# Revit family: console with cutout for bowl without tap hole
name_source: partatom
category: Furniture
units: mm (PartAtom-declared; Revit-internal decimal feet)

## family parameters
Always vertical = No
Cut with Voids When Loaded = No
OmniClass Number = 23.21.19.15.33.13
Room Calculation Point = No
Shared = Yes
Work Plane-Based = No

## types (40) — shared parameters
BIMOBJECT = Sanitary: Compound units
CATALOG = Hansgrohe
DESIGN = Germany
ETIM = EC011381 | Bathroom furniture set
IFC = Furnishing element
MASTERFORMAT = 12 35 30.23 | Bathroom Casework
Manufacturer = Hansgrohe
NBSYN = $BASENUMBER.-$ARTNR.-$SURFACE.-$LODLEVEL.
NN = Console with cutout for bowl without tap hole
OBJECTTYPE = Object (single object)
OMNICLASS = 23-19 31 17 11 | Bathroom Units
PRODUCTFAMILY = Xelu Q
PRODUCTGROUP = console
PRODUCTURL = https://pro.hansgrohe.com
R = 75
REGIONSET = Worldwide
UNICLASS2015 = Pr_40_20_76_94 | Vanity units
UNIFORMATII = E2010 | Fixed Furnishings
UNSPSC = 56 | Furniture and Furnishings

## per-type parameters (varying)
| type | ARTNR | BASENUMBER | GTINCODE | L | LINA | LL | LODLEVEL | Model | NAME | NB | PERMALINK | SPECIFICATION | SURFACE | WEIGHT |
| Console 1180_550 with cutout in the middle for bowl without tap hole-54115050-GLOSSY_WHITE-200 | 54115050 | Console 1180/550 with cutout in the middle for bowl without tap hole | 4059625457450 | 1180 | Console 1180/550 with cutout in the middle for bowl without tap hole-54115050-GLOSSY_WHITE-200 | 590 | 200 | Console 1180/550 with cutout in the middle for bowl without tap hole-54115050-GLOSSY_WHITE-200 | Xelu Q Console 1180/550 with cutout in the middle for bowl without tap hole | Console 1180/550 with cutout in the middle for bowl without tap hole-54115050-GLOSSY_WHITE-200 | 54115XXX | Surfaces:    - 54115050 High Gloss White  - 54115910 Diamond Matt Grey  - 54115230 Natural Oak  - 54115630 Dark Walnut      Specification: | GLOSSY_WHITE | 14.5 |
| Console 1180_550 with cutout in the middle for bowl without tap hole-54115050-GLOSSY_WHITE-400 | 54115050 | Console 1180/550 with cutout in the middle for bowl without tap hole | 4059625457450 | 1180 | Console 1180/550 with cutout in the middle for bowl without tap hole-54115050-GLOSSY_WHITE-400 | 590 | 400 | Console 1180/550 with cutout in the middle for bowl without tap hole-54115050-GLOSSY_WHITE-400 | Xelu Q Console 1180/550 with cutout in the middle for bowl without tap hole | Console 1180/550 with cutout in the middle for bowl without tap hole-54115050-GLOSSY_WHITE-400 | 54115XXX | Surfaces:    - 54115050 High Gloss White  - 54115910 Diamond Matt Grey  - 54115230 Natural Oak  - 54115630 Dark Walnut      Specification: | GLOSSY_WHITE | 14.5 |
| Console 1180_550 with cutout in the middle for bowl without tap hole-54115230-NATURAL_OAK-200 | 54115230 | Console 1180/550 with cutout in the middle for bowl without tap hole | 4059625457450 | 1180 | Console 1180/550 with cutout in the middle for bowl without tap hole-54115230-NATURAL_OAK-200 | 590 | 200 | Console 1180/550 with cutout in the middle for bowl without tap hole-54115230-NATURAL_OAK-200 | Xelu Q Console 1180/550 with cutout in the middle for bowl without tap hole | Console 1180/550 with cutout in the middle for bowl without tap hole-54115230-NATURAL_OAK-200 | 54115XXX | Surfaces:    - 54115050 High Gloss White  - 54115910 Diamond Matt Grey  - 54115230 Natural Oak  - 54115630 Dark Walnut      Specification: | NATURAL_OAK | 14.5 |
| Console 1180_550 with cutout in the middle for bowl without tap hole-54115230-NATURAL_OAK-400 | 54115230 | Console 1180/550 with cutout in the middle for bowl without tap hole | 4059625457450 | 1180 | Console 1180/550 with cutout in the middle for bowl without tap hole-54115230-NATURAL_OAK-400 | 590 | 400 | Console 1180/550 with cutout in the middle for bowl without tap hole-54115230-NATURAL_OAK-400 | Xelu Q Console 1180/550 with cutout in the middle for bowl without tap hole | Console 1180/550 with cutout in the middle for bowl without tap hole-54115230-NATURAL_OAK-400 | 54115XXX | Surfaces:    - 54115050 High Gloss White  - 54115910 Diamond Matt Grey  - 54115230 Natural Oak  - 54115630 Dark Walnut      Specification: | NATURAL_OAK | 14.5 |
| Console 1180_550 with cutout in the middle for bowl without tap hole-54115630-DARK_WALNUT-200 | 54115630 | Console 1180/550 with cutout in the middle for bowl without tap hole | 4059625457450 | 1180 | Console 1180/550 with cutout in the middle for bowl without tap hole-54115630-DARK_WALNUT-200 | 590 | 200 | Console 1180/550 with cutout in the middle for bowl without tap hole-54115630-DARK_WALNUT-200 | Xelu Q Console 1180/550 with cutout in the middle for bowl without tap hole | Console 1180/550 with cutout in the middle for bowl without tap hole-54115630-DARK_WALNUT-200 | 54115XXX | Surfaces:    - 54115050 High Gloss White  - 54115910 Diamond Matt Grey  - 54115230 Natural Oak  - 54115630 Dark Walnut      Specification: | DARK_WALNUT | 14.5 |
| Console 1180_550 with cutout in the middle for bowl without tap hole-54115630-DARK_WALNUT-400 | 54115630 | Console 1180/550 with cutout in the middle for bowl without tap hole | 4059625457450 | 1180 | Console 1180/550 with cutout in the middle for bowl without tap hole-54115630-DARK_WALNUT-400 | 590 | 400 | Console 1180/550 with cutout in the middle for bowl without tap hole-54115630-DARK_WALNUT-400 | Xelu Q Console 1180/550 with cutout in the middle for bowl without tap hole | Console 1180/550 with cutout in the middle for bowl without tap hole-54115630-DARK_WALNUT-400 | 54115XXX | Surfaces:    - 54115050 High Gloss White  - 54115910 Diamond Matt Grey  - 54115230 Natural Oak  - 54115630 Dark Walnut      Specification: | DARK_WALNUT | 14.5 |
| Console 1180_550 with cutout in the middle for bowl without tap hole-54115910-DIAMOND_GREY-200 | 54115910 | Console 1180/550 with cutout in the middle for bowl without tap hole | 4059625457450 | 1180 | Console 1180/550 with cutout in the middle for bowl without tap hole-54115910-DIAMOND_GREY-200 | 590 | 200 | Console 1180/550 with cutout in the middle for bowl without tap hole-54115910-DIAMOND_GREY-200 | Xelu Q Console 1180/550 with cutout in the middle for bowl without tap hole | Console 1180/550 with cutout in the middle for bowl without tap hole-54115910-DIAMOND_GREY-200 | 54115XXX | Surfaces:    - 54115050 High Gloss White  - 54115910 Diamond Matt Grey  - 54115230 Natural Oak  - 54115630 Dark Walnut      Specification: | DIAMOND_GREY | 14.5 |
| Console 1180_550 with cutout in the middle for bowl without tap hole-54115910-DIAMOND_GREY-400 | 54115910 | Console 1180/550 with cutout in the middle for bowl without tap hole | 4059625457450 | 1180 | Console 1180/550 with cutout in the middle for bowl without tap hole-54115910-DIAMOND_GREY-400 | 590 | 400 | Console 1180/550 with cutout in the middle for bowl without tap hole-54115910-DIAMOND_GREY-400 | Xelu Q Console 1180/550 with cutout in the middle for bowl without tap hole | Console 1180/550 with cutout in the middle for bowl without tap hole-54115910-DIAMOND_GREY-400 | 54115XXX | Surfaces:    - 54115050 High Gloss White  - 54115910 Diamond Matt Grey  - 54115230 Natural Oak  - 54115630 Dark Walnut      Specification: | DIAMOND_GREY | 14.5 |
| Console 1360_550 with cutout left for bowl without tap hole-54116050-GLOSSY_WHITE-200 | 54116050 | Console 1360/550 with cutout left for bowl without tap hole | 4059625457818 | 1360 | Console 1360/550 with cutout left for bowl without tap hole-54116050-GLOSSY_WHITE-200 | 340 | 200 | Console 1360/550 with cutout left for bowl without tap hole-54116050-GLOSSY_WHITE-200 | Xelu Q Console 1360/550 with cutout left for bowl without tap hole | Console 1360/550 with cutout left for bowl without tap hole-54116050-GLOSSY_WHITE-200 | 54116XXX | Surfaces:    - 54116050 High Gloss White  - 54116910 Diamond Matt Grey  - 54116230 Natural Oak  - 54116630 Dark Walnut      Specification: | GLOSSY_WHITE | 12.2 |
| Console 1360_550 with cutout left for bowl without tap hole-54116050-GLOSSY_WHITE-400 | 54116050 | Console 1360/550 with cutout left for bowl without tap hole | 4059625457818 | 1360 | Console 1360/550 with cutout left for bowl without tap hole-54116050-GLOSSY_WHITE-400 | 340 | 400 | Console 1360/550 with cutout left for bowl without tap hole-54116050-GLOSSY_WHITE-400 | Xelu Q Console 1360/550 with cutout left for bowl without tap hole | Console 1360/550 with cutout left for bowl without tap hole-54116050-GLOSSY_WHITE-400 | 54116XXX | Surfaces:    - 54116050 High Gloss White  - 54116910 Diamond Matt Grey  - 54116230 Natural Oak  - 54116630 Dark Walnut      Specification: | GLOSSY_WHITE | 12.2 |
| Console 1360_550 with cutout left for bowl without tap hole-54116230-NATURAL_OAK-200 | 54116230 | Console 1360/550 with cutout left for bowl without tap hole | 4059625457818 | 1360 | Console 1360/550 with cutout left for bowl without tap hole-54116230-NATURAL_OAK-200 | 340 | 200 | Console 1360/550 with cutout left for bowl without tap hole-54116230-NATURAL_OAK-200 | Xelu Q Console 1360/550 with cutout left for bowl without tap hole | Console 1360/550 with cutout left for bowl without tap hole-54116230-NATURAL_OAK-200 | 54116XXX | Surfaces:    - 54116050 High Gloss White  - 54116910 Diamond Matt Grey  - 54116230 Natural Oak  - 54116630 Dark Walnut      Specification: | NATURAL_OAK | 12.2 |
| Console 1360_550 with cutout left for bowl without tap hole-54116230-NATURAL_OAK-400 | 54116230 | Console 1360/550 with cutout left for bowl without tap hole | 4059625457818 | 1360 | Console 1360/550 with cutout left for bowl without tap hole-54116230-NATURAL_OAK-400 | 340 | 400 | Console 1360/550 with cutout left for bowl without tap hole-54116230-NATURAL_OAK-400 | Xelu Q Console 1360/550 with cutout left for bowl without tap hole | Console 1360/550 with cutout left for bowl without tap hole-54116230-NATURAL_OAK-400 | 54116XXX | Surfaces:    - 54116050 High Gloss White  - 54116910 Diamond Matt Grey  - 54116230 Natural Oak  - 54116630 Dark Walnut      Specification: | NATURAL_OAK | 12.2 |
| Console 1360_550 with cutout left for bowl without tap hole-54116630-DARK_WALNUT-200 | 54116630 | Console 1360/550 with cutout left for bowl without tap hole | 4059625457818 | 1360 | Console 1360/550 with cutout left for bowl without tap hole-54116630-DARK_WALNUT-200 | 340 | 200 | Console 1360/550 with cutout left for bowl without tap hole-54116630-DARK_WALNUT-200 | Xelu Q Console 1360/550 with cutout left for bowl without tap hole | Console 1360/550 with cutout left for bowl without tap hole-54116630-DARK_WALNUT-200 | 54116XXX | Surfaces:    - 54116050 High Gloss White  - 54116910 Diamond Matt Grey  - 54116230 Natural Oak  - 54116630 Dark Walnut      Specification: | DARK_WALNUT | 12.2 |
| Console 1360_550 with cutout left for bowl without tap hole-54116630-DARK_WALNUT-400 | 54116630 | Console 1360/550 with cutout left for bowl without tap hole | 4059625457818 | 1360 | Console 1360/550 with cutout left for bowl without tap hole-54116630-DARK_WALNUT-400 | 340 | 400 | Console 1360/550 with cutout left for bowl without tap hole-54116630-DARK_WALNUT-400 | Xelu Q Console 1360/550 with cutout left for bowl without tap hole | Console 1360/550 with cutout left for bowl without tap hole-54116630-DARK_WALNUT-400 | 54116XXX | Surfaces:    - 54116050 High Gloss White  - 54116910 Diamond Matt Grey  - 54116230 Natural Oak  - 54116630 Dark Walnut      Specification: | DARK_WALNUT | 12.2 |
| Console 1360_550 with cutout left for bowl without tap hole-54116910-DIAMOND_GREY-200 | 54116910 | Console 1360/550 with cutout left for bowl without tap hole | 4059625457818 | 1360 | Console 1360/550 with cutout left for bowl without tap hole-54116910-DIAMOND_GREY-200 | 340 | 200 | Console 1360/550 with cutout left for bowl without tap hole-54116910-DIAMOND_GREY-200 | Xelu Q Console 1360/550 with cutout left for bowl without tap hole | Console 1360/550 with cutout left for bowl without tap hole-54116910-DIAMOND_GREY-200 | 54116XXX | Surfaces:    - 54116050 High Gloss White  - 54116910 Diamond Matt Grey  - 54116230 Natural Oak  - 54116630 Dark Walnut      Specification: | DIAMOND_GREY | 12.2 |
| Console 1360_550 with cutout left for bowl without tap hole-54116910-DIAMOND_GREY-400 | 54116910 | Console 1360/550 with cutout left for bowl without tap hole | 4059625457818 | 1360 | Console 1360/550 with cutout left for bowl without tap hole-54116910-DIAMOND_GREY-400 | 340 | 400 | Console 1360/550 with cutout left for bowl without tap hole-54116910-DIAMOND_GREY-400 | Xelu Q Console 1360/550 with cutout left for bowl without tap hole | Console 1360/550 with cutout left for bowl without tap hole-54116910-DIAMOND_GREY-400 | 54116XXX | Surfaces:    - 54116050 High Gloss White  - 54116910 Diamond Matt Grey  - 54116230 Natural Oak  - 54116630 Dark Walnut      Specification: | DIAMOND_GREY | 12.2 |
| Console 1360_550 with cutout right for bowl without tap hole-54117050-GLOSSY_WHITE-200 | 54117050 | Console 1360/550 with cutout right for bowl without tap hole | 4059625457771 | 1360 | Console 1360/550 with cutout right for bowl without tap hole-54117050-GLOSSY_WHITE-200 | 1020 | 200 | Console 1360/550 with cutout right for bowl without tap hole-54117050-GLOSSY_WHITE-200 | Xelu Q Console 1360/550 with cutout right for bowl without tap hole | Console 1360/550 with cutout right for bowl without tap hole-54117050-GLOSSY_WHITE-200 | 54117XXX | Surfaces:    - 54117050 High Gloss White  - 54117910 Diamond Matt Grey  - 54117230 Natural Oak  - 54117630 Dark Walnut      Specification: | GLOSSY_WHITE | 12.2 |
| Console 1360_550 with cutout right for bowl without tap hole-54117050-GLOSSY_WHITE-400 | 54117050 | Console 1360/550 with cutout right for bowl without tap hole | 4059625457771 | 1360 | Console 1360/550 with cutout right for bowl without tap hole-54117050-GLOSSY_WHITE-400 | 1020 | 400 | Console 1360/550 with cutout right for bowl without tap hole-54117050-GLOSSY_WHITE-400 | Xelu Q Console 1360/550 with cutout right for bowl without tap hole | Console 1360/550 with cutout right for bowl without tap hole-54117050-GLOSSY_WHITE-400 | 54117XXX | Surfaces:    - 54117050 High Gloss White  - 54117910 Diamond Matt Grey  - 54117230 Natural Oak  - 54117630 Dark Walnut      Specification: | GLOSSY_WHITE | 12.2 |
| Console 1360_550 with cutout right for bowl without tap hole-54117230-NATURAL_OAK-200 | 54117230 | Console 1360/550 with cutout right for bowl without tap hole | 4059625457771 | 1360 | Console 1360/550 with cutout right for bowl without tap hole-54117230-NATURAL_OAK-200 | 1020 | 200 | Console 1360/550 with cutout right for bowl without tap hole-54117230-NATURAL_OAK-200 | Xelu Q Console 1360/550 with cutout right for bowl without tap hole | Console 1360/550 with cutout right for bowl without tap hole-54117230-NATURAL_OAK-200 | 54117XXX | Surfaces:    - 54117050 High Gloss White  - 54117910 Diamond Matt Grey  - 54117230 Natural Oak  - 54117630 Dark Walnut      Specification: | NATURAL_OAK | 12.2 |
| Console 1360_550 with cutout right for bowl without tap hole-54117230-NATURAL_OAK-400 | 54117230 | Console 1360/550 with cutout right for bowl without tap hole | 4059625457771 | 1360 | Console 1360/550 with cutout right for bowl without tap hole-54117230-NATURAL_OAK-400 | 1020 | 400 | Console 1360/550 with cutout right for bowl without tap hole-54117230-NATURAL_OAK-400 | Xelu Q Console 1360/550 with cutout right for bowl without tap hole | Console 1360/550 with cutout right for bowl without tap hole-54117230-NATURAL_OAK-400 | 54117XXX | Surfaces:    - 54117050 High Gloss White  - 54117910 Diamond Matt Grey  - 54117230 Natural Oak  - 54117630 Dark Walnut      Specification: | NATURAL_OAK | 12.2 |
| Console 1360_550 with cutout right for bowl without tap hole-54117630-DARK_WALNUT-200 | 54117630 | Console 1360/550 with cutout right for bowl without tap hole | 4059625457771 | 1360 | Console 1360/550 with cutout right for bowl without tap hole-54117630-DARK_WALNUT-200 | 1020 | 200 | Console 1360/550 with cutout right for bowl without tap hole-54117630-DARK_WALNUT-200 | Xelu Q Console 1360/550 with cutout right for bowl without tap hole | Console 1360/550 with cutout right for bowl without tap hole-54117630-DARK_WALNUT-200 | 54117XXX | Surfaces:    - 54117050 High Gloss White  - 54117910 Diamond Matt Grey  - 54117230 Natural Oak  - 54117630 Dark Walnut      Specification: | DARK_WALNUT | 12.2 |
| Console 1360_550 with cutout right for bowl without tap hole-54117630-DARK_WALNUT-400 | 54117630 | Console 1360/550 with cutout right for bowl without tap hole | 4059625457771 | 1360 | Console 1360/550 with cutout right for bowl without tap hole-54117630-DARK_WALNUT-400 | 1020 | 400 | Console 1360/550 with cutout right for bowl without tap hole-54117630-DARK_WALNUT-400 | Xelu Q Console 1360/550 with cutout right for bowl without tap hole | Console 1360/550 with cutout right for bowl without tap hole-54117630-DARK_WALNUT-400 | 54117XXX | Surfaces:    - 54117050 High Gloss White  - 54117910 Diamond Matt Grey  - 54117230 Natural Oak  - 54117630 Dark Walnut      Specification: | DARK_WALNUT | 12.2 |
| Console 1360_550 with cutout right for bowl without tap hole-54117910-DIAMOND_GREY-200 | 54117910 | Console 1360/550 with cutout right for bowl without tap hole | 4059625457771 | 1360 | Console 1360/550 with cutout right for bowl without tap hole-54117910-DIAMOND_GREY-200 | 1020 | 200 | Console 1360/550 with cutout right for bowl without tap hole-54117910-DIAMOND_GREY-200 | Xelu Q Console 1360/550 with cutout right for bowl without tap hole | Console 1360/550 with cutout right for bowl without tap hole-54117910-DIAMOND_GREY-200 | 54117XXX | Surfaces:    - 54117050 High Gloss White  - 54117910 Diamond Matt Grey  - 54117230 Natural Oak  - 54117630 Dark Walnut      Specification: | DIAMOND_GREY | 12.2 |
| Console 1360_550 with cutout right for bowl without tap hole-54117910-DIAMOND_GREY-400 | 54117910 | Console 1360/550 with cutout right for bowl without tap hole | 4059625457771 | 1360 | Console 1360/550 with cutout right for bowl without tap hole-54117910-DIAMOND_GREY-400 | 1020 | 400 | Console 1360/550 with cutout right for bowl without tap hole-54117910-DIAMOND_GREY-400 | Xelu Q Console 1360/550 with cutout right for bowl without tap hole | Console 1360/550 with cutout right for bowl without tap hole-54117910-DIAMOND_GREY-400 | 54117XXX | Surfaces:    - 54117050 High Gloss White  - 54117910 Diamond Matt Grey  - 54117230 Natural Oak  - 54117630 Dark Walnut      Specification: | DIAMOND_GREY | 12.2 |
| Console 780_550 with cutout in the middle for bowl without tap hole-54113050-GLOSSY_WHITE-200 | 54113050 | Console 780/550 with cutout in the middle for bowl without tap hole | 4059625457535 | 780 | Console 780/550 with cutout in the middle for bowl without tap hole-54113050-GLOSSY_WHITE-200 | 390 | 200 | Console 780/550 with cutout in the middle for bowl without tap hole-54113050-GLOSSY_WHITE-200 | Xelu Q Console 780/550 with cutout in the middle for bowl without tap hole | Console 780/550 with cutout in the middle for bowl without tap hole-54113050-GLOSSY_WHITE-200 | 54113XXX | Surfaces:    - 54113050 High Gloss White  - 54113910 Diamond Matt Grey  - 54113230 Natural Oak  - 54113630 Dark Walnut      Specification: | GLOSSY_WHITE | 8.4 |
| Console 780_550 with cutout in the middle for bowl without tap hole-54113050-GLOSSY_WHITE-400 | 54113050 | Console 780/550 with cutout in the middle for bowl without tap hole | 4059625457535 | 780 | Console 780/550 with cutout in the middle for bowl without tap hole-54113050-GLOSSY_WHITE-400 | 390 | 400 | Console 780/550 with cutout in the middle for bowl without tap hole-54113050-GLOSSY_WHITE-400 | Xelu Q Console 780/550 with cutout in the middle for bowl without tap hole | Console 780/550 with cutout in the middle for bowl without tap hole-54113050-GLOSSY_WHITE-400 | 54113XXX | Surfaces:    - 54113050 High Gloss White  - 54113910 Diamond Matt Grey  - 54113230 Natural Oak  - 54113630 Dark Walnut      Specification: | GLOSSY_WHITE | 8.4 |
| Console 780_550 with cutout in the middle for bowl without tap hole-54113230-NATURAL_OAK-200 | 54113230 | Console 780/550 with cutout in the middle for bowl without tap hole | 4059625457535 | 780 | Console 780/550 with cutout in the middle for bowl without tap hole-54113230-NATURAL_OAK-200 | 390 | 200 | Console 780/550 with cutout in the middle for bowl without tap hole-54113230-NATURAL_OAK-200 | Xelu Q Console 780/550 with cutout in the middle for bowl without tap hole | Console 780/550 with cutout in the middle for bowl without tap hole-54113230-NATURAL_OAK-200 | 54113XXX | Surfaces:    - 54113050 High Gloss White  - 54113910 Diamond Matt Grey  - 54113230 Natural Oak  - 54113630 Dark Walnut      Specification: | NATURAL_OAK | 8.4 |
| Console 780_550 with cutout in the middle for bowl without tap hole-54113230-NATURAL_OAK-400 | 54113230 | Console 780/550 with cutout in the middle for bowl without tap hole | 4059625457535 | 780 | Console 780/550 with cutout in the middle for bowl without tap hole-54113230-NATURAL_OAK-400 | 390 | 400 | Console 780/550 with cutout in the middle for bowl without tap hole-54113230-NATURAL_OAK-400 | Xelu Q Console 780/550 with cutout in the middle for bowl without tap hole | Console 780/550 with cutout in the middle for bowl without tap hole-54113230-NATURAL_OAK-400 | 54113XXX | Surfaces:    - 54113050 High Gloss White  - 54113910 Diamond Matt Grey  - 54113230 Natural Oak  - 54113630 Dark Walnut      Specification: | NATURAL_OAK | 8.4 |
| Console 780_550 with cutout in the middle for bowl without tap hole-54113630-DARK_WALNUT-200 | 54113630 | Console 780/550 with cutout in the middle for bowl without tap hole | 4059625457535 | 780 | Console 780/550 with cutout in the middle for bowl without tap hole-54113630-DARK_WALNUT-200 | 390 | 200 | Console 780/550 with cutout in the middle for bowl without tap hole-54113630-DARK_WALNUT-200 | Xelu Q Console 780/550 with cutout in the middle for bowl without tap hole | Console 780/550 with cutout in the middle for bowl without tap hole-54113630-DARK_WALNUT-200 | 54113XXX | Surfaces:    - 54113050 High Gloss White  - 54113910 Diamond Matt Grey  - 54113230 Natural Oak  - 54113630 Dark Walnut      Specification: | DARK_WALNUT | 8.4 |
| Console 780_550 with cutout in the middle for bowl without tap hole-54113630-DARK_WALNUT-400 | 54113630 | Console 780/550 with cutout in the middle for bowl without tap hole | 4059625457535 | 780 | Console 780/550 with cutout in the middle for bowl without tap hole-54113630-DARK_WALNUT-400 | 390 | 400 | Console 780/550 with cutout in the middle for bowl without tap hole-54113630-DARK_WALNUT-400 | Xelu Q Console 780/550 with cutout in the middle for bowl without tap hole | Console 780/550 with cutout in the middle for bowl without tap hole-54113630-DARK_WALNUT-400 | 54113XXX | Surfaces:    - 54113050 High Gloss White  - 54113910 Diamond Matt Grey  - 54113230 Natural Oak  - 54113630 Dark Walnut      Specification: | DARK_WALNUT | 8.4 |
| Console 780_550 with cutout in the middle for bowl without tap hole-54113910-DIAMOND_GREY-200 | 54113910 | Console 780/550 with cutout in the middle for bowl without tap hole | 4059625457535 | 780 | Console 780/550 with cutout in the middle for bowl without tap hole-54113910-DIAMOND_GREY-200 | 390 | 200 | Console 780/550 with cutout in the middle for bowl without tap hole-54113910-DIAMOND_GREY-200 | Xelu Q Console 780/550 with cutout in the middle for bowl without tap hole | Console 780/550 with cutout in the middle for bowl without tap hole-54113910-DIAMOND_GREY-200 | 54113XXX | Surfaces:    - 54113050 High Gloss White  - 54113910 Diamond Matt Grey  - 54113230 Natural Oak  - 54113630 Dark Walnut      Specification: | DIAMOND_GREY | 8.4 |
| Console 780_550 with cutout in the middle for bowl without tap hole-54113910-DIAMOND_GREY-400 | 54113910 | Console 780/550 with cutout in the middle for bowl without tap hole | 4059625457535 | 780 | Console 780/550 with cutout in the middle for bowl without tap hole-54113910-DIAMOND_GREY-400 | 390 | 400 | Console 780/550 with cutout in the middle for bowl without tap hole-54113910-DIAMOND_GREY-400 | Xelu Q Console 780/550 with cutout in the middle for bowl without tap hole | Console 780/550 with cutout in the middle for bowl without tap hole-54113910-DIAMOND_GREY-400 | 54113XXX | Surfaces:    - 54113050 High Gloss White  - 54113910 Diamond Matt Grey  - 54113230 Natural Oak  - 54113630 Dark Walnut      Specification: | DIAMOND_GREY | 8.4 |
| Console 980_550 with cutout in the middle for bowl without tap hole-54114050-GLOSSY_WHITE-200 | 54114050 | Console 980/550 with cutout in the middle for bowl without tap hole | 4059625457498 | 980 | Console 980/550 with cutout in the middle for bowl without tap hole-54114050-GLOSSY_WHITE-200 | 490 | 200 | Console 980/550 with cutout in the middle for bowl without tap hole-54114050-GLOSSY_WHITE-200 | Xelu Q Console 980/550 with cutout in the middle for bowl without tap hole | Console 980/550 with cutout in the middle for bowl without tap hole-54114050-GLOSSY_WHITE-200 | 54114XXX | Surfaces:    - 54114050 High Gloss White  - 54114910 Diamond Matt Grey  - 54114230 Natural Oak  - 54114630 Dark Walnut      Specification: | GLOSSY_WHITE | 13.2 |
| Console 980_550 with cutout in the middle for bowl without tap hole-54114050-GLOSSY_WHITE-400 | 54114050 | Console 980/550 with cutout in the middle for bowl without tap hole | 4059625457498 | 980 | Console 980/550 with cutout in the middle for bowl without tap hole-54114050-GLOSSY_WHITE-400 | 490 | 400 | Console 980/550 with cutout in the middle for bowl without tap hole-54114050-GLOSSY_WHITE-400 | Xelu Q Console 980/550 with cutout in the middle for bowl without tap hole | Console 980/550 with cutout in the middle for bowl without tap hole-54114050-GLOSSY_WHITE-400 | 54114XXX | Surfaces:    - 54114050 High Gloss White  - 54114910 Diamond Matt Grey  - 54114230 Natural Oak  - 54114630 Dark Walnut      Specification: | GLOSSY_WHITE | 13.2 |
| Console 980_550 with cutout in the middle for bowl without tap hole-54114230-NATURAL_OAK-200 | 54114230 | Console 980/550 with cutout in the middle for bowl without tap hole | 4059625457498 | 980 | Console 980/550 with cutout in the middle for bowl without tap hole-54114230-NATURAL_OAK-200 | 490 | 200 | Console 980/550 with cutout in the middle for bowl without tap hole-54114230-NATURAL_OAK-200 | Xelu Q Console 980/550 with cutout in the middle for bowl without tap hole | Console 980/550 with cutout in the middle for bowl without tap hole-54114230-NATURAL_OAK-200 | 54114XXX | Surfaces:    - 54114050 High Gloss White  - 54114910 Diamond Matt Grey  - 54114230 Natural Oak  - 54114630 Dark Walnut      Specification: | NATURAL_OAK | 13.2 |
| Console 980_550 with cutout in the middle for bowl without tap hole-54114230-NATURAL_OAK-400 | 54114230 | Console 980/550 with cutout in the middle for bowl without tap hole | 4059625457498 | 980 | Console 980/550 with cutout in the middle for bowl without tap hole-54114230-NATURAL_OAK-400 | 490 | 400 | Console 980/550 with cutout in the middle for bowl without tap hole-54114230-NATURAL_OAK-400 | Xelu Q Console 980/550 with cutout in the middle for bowl without tap hole | Console 980/550 with cutout in the middle for bowl without tap hole-54114230-NATURAL_OAK-400 | 54114XXX | Surfaces:    - 54114050 High Gloss White  - 54114910 Diamond Matt Grey  - 54114230 Natural Oak  - 54114630 Dark Walnut      Specification: | NATURAL_OAK | 13.2 |
| Console 980_550 with cutout in the middle for bowl without tap hole-54114630-DARK_WALNUT-200 | 54114630 | Console 980/550 with cutout in the middle for bowl without tap hole | 4059625457498 | 980 | Console 980/550 with cutout in the middle for bowl without tap hole-54114630-DARK_WALNUT-200 | 490 | 200 | Console 980/550 with cutout in the middle for bowl without tap hole-54114630-DARK_WALNUT-200 | Xelu Q Console 980/550 with cutout in the middle for bowl without tap hole | Console 980/550 with cutout in the middle for bowl without tap hole-54114630-DARK_WALNUT-200 | 54114XXX | Surfaces:    - 54114050 High Gloss White  - 54114910 Diamond Matt Grey  - 54114230 Natural Oak  - 54114630 Dark Walnut      Specification: | DARK_WALNUT | 13.2 |
| Console 980_550 with cutout in the middle for bowl without tap hole-54114630-DARK_WALNUT-400 | 54114630 | Console 980/550 with cutout in the middle for bowl without tap hole | 4059625457498 | 980 | Console 980/550 with cutout in the middle for bowl without tap hole-54114630-DARK_WALNUT-400 | 490 | 400 | Console 980/550 with cutout in the middle for bowl without tap hole-54114630-DARK_WALNUT-400 | Xelu Q Console 980/550 with cutout in the middle for bowl without tap hole | Console 980/550 with cutout in the middle for bowl without tap hole-54114630-DARK_WALNUT-400 | 54114XXX | Surfaces:    - 54114050 High Gloss White  - 54114910 Diamond Matt Grey  - 54114230 Natural Oak  - 54114630 Dark Walnut      Specification: | DARK_WALNUT | 13.2 |
| Console 980_550 with cutout in the middle for bowl without tap hole-54114910-DIAMOND_GREY-200 | 54114910 | Console 980/550 with cutout in the middle for bowl without tap hole | 4059625457498 | 980 | Console 980/550 with cutout in the middle for bowl without tap hole-54114910-DIAMOND_GREY-200 | 490 | 200 | Console 980/550 with cutout in the middle for bowl without tap hole-54114910-DIAMOND_GREY-200 | Xelu Q Console 980/550 with cutout in the middle for bowl without tap hole | Console 980/550 with cutout in the middle for bowl without tap hole-54114910-DIAMOND_GREY-200 | 54114XXX | Surfaces:    - 54114050 High Gloss White  - 54114910 Diamond Matt Grey  - 54114230 Natural Oak  - 54114630 Dark Walnut      Specification: | DIAMOND_GREY | 13.2 |
| Console 980_550 with cutout in the middle for bowl without tap hole-54114910-DIAMOND_GREY-400 | 54114910 | Console 980/550 with cutout in the middle for bowl without tap hole | 4059625457498 | 980 | Console 980/550 with cutout in the middle for bowl without tap hole-54114910-DIAMOND_GREY-400 | 490 | 400 | Console 980/550 with cutout in the middle for bowl without tap hole-54114910-DIAMOND_GREY-400 | Xelu Q Console 980/550 with cutout in the middle for bowl without tap hole | Console 980/550 with cutout in the middle for bowl without tap hole-54114910-DIAMOND_GREY-400 | 54114XXX | Surfaces:    - 54114050 High Gloss White  - 54114910 Diamond Matt Grey  - 54114230 Natural Oak  - 54114630 Dark Walnut      Specification: | DIAMOND_GREY | 13.2 |

type visibility flags: 40 boolean params named "<type name>_RX0RY0RZ0TX0TY0TZ0_V" — each type sets only its own to Yes (folded from table)

## geometry (parser evidence)
native form markers: Sweep x95
no freeform markers — native parametric forms only
